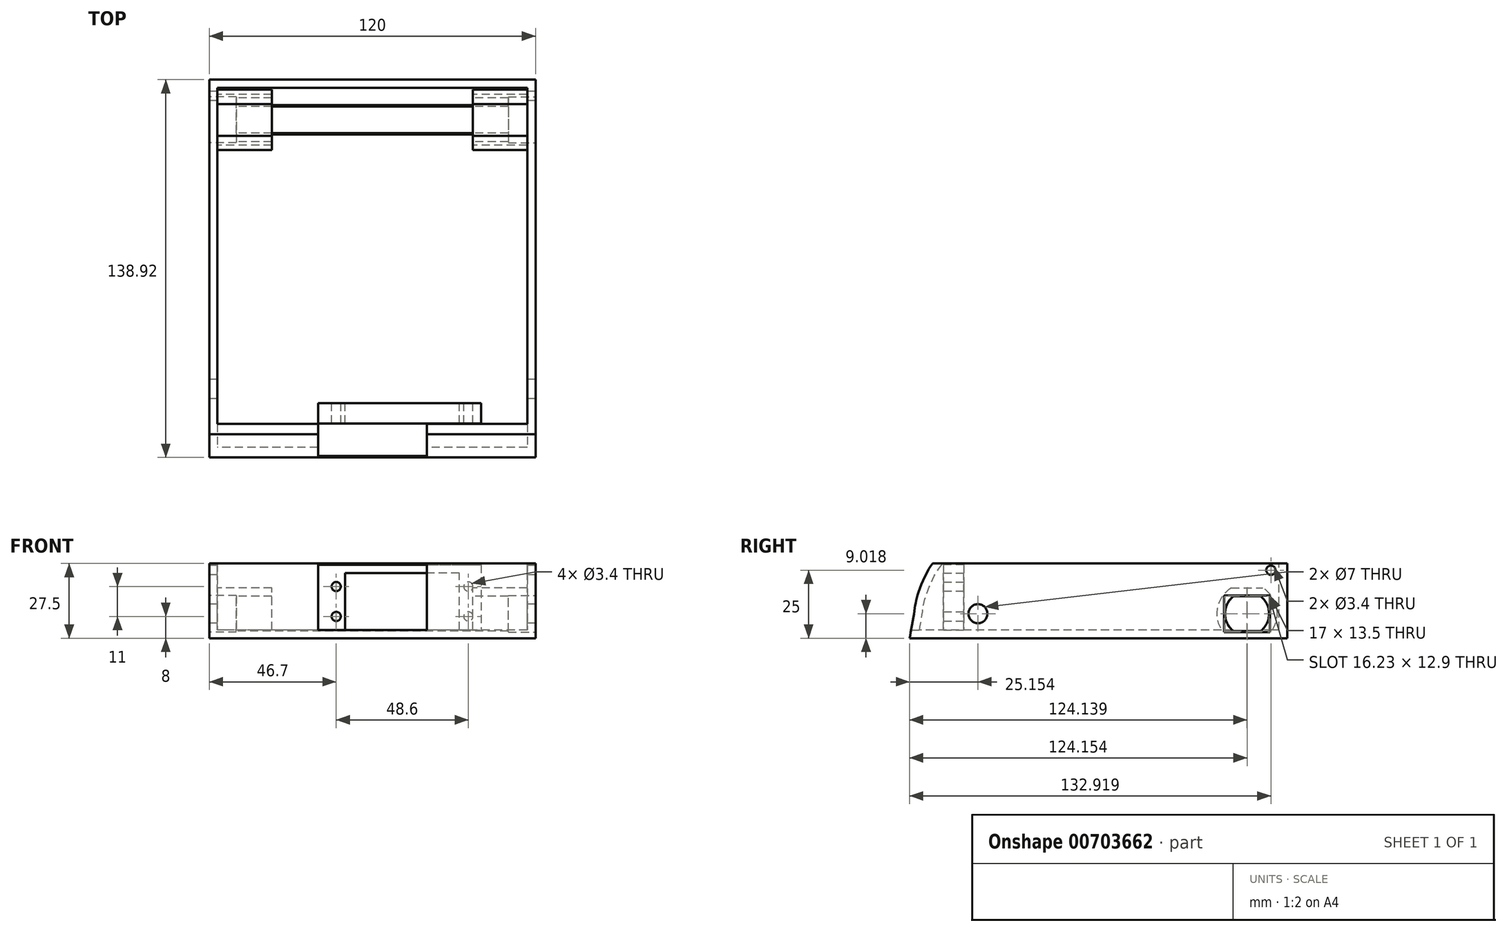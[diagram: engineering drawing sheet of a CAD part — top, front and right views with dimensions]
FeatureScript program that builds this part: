
annotation { "Feature Type Name" : "Feature", "Feature Type Description" : "" }
export const myFeature = defineFeature(function(context is Context, id is Id, definition is map)
    precondition{}
    {
        {
            var Q0;
            Q0=qCreatedBy(makeId("Right.planeOp"),FACE);
            var sketch = newSketch(context, id + "F0", { "sketchPlane" : qUnion([Q0])});
            skLineSegment(sketch, "E0", {"start": v(-41, 0) * mm, "end": v(-40.96, 0) * mm});
            skLineSegment(sketch, "E1", {"start": v(97.96, 0) * mm, "end": v(97.96, 27.5) * mm});
            skLineSegment(sketch, "E2", {"start": v(83.2, 9.02) * mm, "end": v(-15.8, 9.02) * mm, "construction": true});
            skPoint(sketch, "E3", {"position": v(-15.8, 9.02) * mm});
            skLineSegment(sketch, "E4", {"start": v(78.27, 15.47) * mm, "end": v(88.1, 15.47) * mm});
            skLineSegment(sketch, "E5", {"start": v(88.1, 15.47) * mm, "end": v(88.1, 2.57) * mm, "construction": true});
            skLineSegment(sketch, "E6", {"start": v(88.1, 2.57) * mm, "end": v(78.27, 2.57) * mm});
            skArc(sketch, "E7", {"start": v(88.1, 2.57) * mm, "mid": v(91.3, 9.02) * mm, "end": v(88.1, 15.47) * mm});
            skArc(sketch, "E8", {"start": v(78.27, 15.47) * mm, "mid": v(75.07, 9.02) * mm, "end": v(78.27, 2.57) * mm});
            skPoint(sketch, "E9", {"position": v(91.96, 25) * mm});
            skLineSegment(sketch, "E10.bottom", {"start": v(97.96, 27.5) * mm, "end": v(-28.02, 27.5) * mm});
            skLineSegment(sketch, "E10.top", {"start": v(97.96, 0) * mm, "end": v(-32.25, 0) * mm});
            skLineSegment(sketch, "E10.left", {"start": v(97.96, 27.5) * mm, "end": v(97.96, 0) * mm});
            skLineSegment(sketch, "E11.bottom", {"start": v(97.96, 27.5) * mm, "end": v(91.96, 27.5) * mm, "construction": true});
            skLineSegment(sketch, "E11.top", {"start": v(97.96, 25) * mm, "end": v(91.96, 25) * mm, "construction": true});
            skLineSegment(sketch, "E11.left", {"start": v(97.96, 27.5) * mm, "end": v(97.96, 25) * mm, "construction": true});
            skLineSegment(sketch, "E11.right", {"start": v(91.96, 27.5) * mm, "end": v(91.96, 25) * mm, "construction": true});
            skLineSegment(sketch, "E12.trimOffspring", {"start": v(-32.25, 0) * mm, "end": v(97.96, 0) * mm});
            skLineSegment(sketch, "E13", {"start": v(-28.02, 27.5) * mm, "end": v(-32.48, 27.5) * mm});
            skFitSpline(sketch, "E14.trimOffspring", {"points": [v(-39.2, 9.98) * mm, v(-16.17, 42.26) * mm, v(13.43, 34.63) * mm, v(52.81, 46.98) * mm, v(101.54, 39.4) * mm], "startDerivative": vector(14.6, 154.8) * mm, "endDerivative": vector(82.89, -42.84) * mm, "construction": true});
            skFitSpline(sketch, "E15", {"points": [v(-32.48, 27.5) * mm, v(-37.99, 15.88) * mm, v(-39.2, 9.98) * mm, v(-40.96, 0) * mm], "startDerivative": vector(-16.4, -20.95) * mm, "endDerivative": vector(-4.3, -20.78) * mm});
            skLineSegment(sketch, "E16", {"start": v(-40.96, 0) * mm, "end": v(-32.25, 0) * mm});
            skLineSegment(sketch, "E17.bottom", {"start": v(-40.96, 0) * mm, "end": v(-35.91, 0) * mm});
            skSolve(sketch);
        }
        {
            var Q0;
            Q0=makeQuery(id+"F0.imprint","IMPRINT",FACE,{"disambiguationData":[TD([[makeQuery(id+"F0.imprint","IMPRINT",EDGE,{"derivedFrom":sQuery(id+"F0.wireOp",EDGE,"E4")}),1.0]])]});
            var Q1;
            {var subQ0=sQuery(id+"F0.wireOp",EDGE,"E17.bottom");Q1=makeQuery(id+"F0.imprint","IMPRINT",FACE,{"disambiguationData":[TD([[makeQuery(id+"F0.imprint","IMPRINT",EDGE,{"derivedFrom":subQ0}),1.0]])]});}
            extrude(context, id + "F1", {"entities" : qUnion([Q0, Q1]), "depth" : 120 * mm, "offsetDistance" : 25.4 * mm});
        }
        {
            var Q0;
            Q0=makeQuery(id+"F1.opExtrude","SWEPT_FACE",FACE,{"disambiguationData":[OSD([sQuery(id+"F0.wireOp",EDGE,"E10.bottom")])]});
            shell(context, id + "F2", {"entities" : qUnion([Q0]), "thickness" : 3 * mm});
        }
        {
            var Q0;
            Q0=sQuery(id+"F0.wireOp",VERTEX,"E3");
            var Q1;
            Q1=makeQuery(id+"F1.opExtrude","SWEPT_BODY",BODY,{"disambiguationData":[OSD([sQuery(id+"F0.wireOp",EDGE,"E4"),sQuery(id+"F0.wireOp",EDGE,"E6"),sQuery(id+"F0.wireOp",EDGE,"E7"),sQuery(id+"F0.wireOp",EDGE,"E8"),sQuery(id+"F0.wireOp",EDGE,"E10.bottom"),sQuery(id+"F0.wireOp",EDGE,"E10.top"),sQuery(id+"F0.wireOp",EDGE,"E10.left"),sQuery(id+"F0.wireOp",EDGE,"E10.right")])]});
            hole(context, id + "F3", {"style" : HoleStyle.SIMPLE, "endStyle" : HoleEndStyle.BLIND, "oppositeDirection" : true, "holeDiameter" : 7 * mm, "majorDiameter" : 5 * mm, "holeDepth" : 200 * mm, "isTappedThrough" : true, "tappedDepth" : 12 * mm, "tapClearance" : 3, "locations" : qUnion([Q0]), "scope" : qUnion([Q1])});
        }
        {
            var Q0;
            Q0=sQuery(id+"F0.wireOp",VERTEX,"E9");
            var Q1;
            Q1=makeQuery(id+"F1.opExtrude","SWEPT_BODY",BODY,{"disambiguationData":[OSD([sQuery(id+"F0.wireOp",EDGE,"E0"),sQuery(id+"F0.wireOp",EDGE,"E1"),sQuery(id+"F0.wireOp",EDGE,"acc88329-f66e-44b0-b4c6-be808748104b"),sQuery(id+"F0.wireOp",EDGE,"9b4011fb-e8ac-4986-8edf-912ef74731e7.bottom"),sQuery(id+"F0.wireOp",EDGE,"E4"),sQuery(id+"F0.wireOp",EDGE,"E6"),sQuery(id+"F0.wireOp",EDGE,"E7"),sQuery(id+"F0.wireOp",EDGE,"E8")])]});
            hole(context, id + "F4", {"style" : HoleStyle.SIMPLE, "endStyle" : HoleEndStyle.BLIND, "oppositeDirection" : true, "holeDiameter" : 3.4 * mm, "majorDiameter" : 5 * mm, "holeDepth" : 200 * mm, "isTappedThrough" : true, "tappedDepth" : 12 * mm, "tapClearance" : 3, "locations" : qUnion([Q0]), "scope" : qUnion([Q1])});
        }
        {
            var Q0;
            Q0=makeQuery(id+"F1.opExtrude","CAP_FACE",FACE,{"disambiguationData":[OSD([sQuery(id+"F0.wireOp",EDGE,"E0"),sQuery(id+"F0.wireOp",EDGE,"E1"),sQuery(id+"F0.wireOp",EDGE,"acc88329-f66e-44b0-b4c6-be808748104b"),sQuery(id+"F0.wireOp",EDGE,"9b4011fb-e8ac-4986-8edf-912ef74731e7.bottom"),sQuery(id+"F0.wireOp",EDGE,"E4"),sQuery(id+"F0.wireOp",EDGE,"E6"),sQuery(id+"F0.wireOp",EDGE,"E7"),sQuery(id+"F0.wireOp",EDGE,"E8")])],"isStart":false});
            var sketch = newSketch(context, id + "F5", { "sketchPlane" : qUnion([Q0])});
            skLineSegment(sketch, "E18.bottom", {"start": v(91.7, 2.27) * mm, "end": v(74.7, 2.27) * mm});
            skLineSegment(sketch, "E18.top", {"start": v(91.7, 15.77) * mm, "end": v(74.7, 15.77) * mm});
            skLineSegment(sketch, "E18.left", {"start": v(91.7, 2.27) * mm, "end": v(91.7, 15.77) * mm});
            skLineSegment(sketch, "E18.right", {"start": v(74.7, 2.27) * mm, "end": v(74.7, 15.77) * mm});
            skPoint(sketch, "E18.middle", {"position": v(83.2, 9.02) * mm});
            skSolve(sketch);
        }
        {
            var Q0;
            Q0=qSketchRegion(id+"F5",true);
            extrude(context, id + "F6", {"entities" : qUnion([Q0]), "operationType" : NewBodyOperationType.REMOVE, "oppositeDirection" : true, "depth" : 10 * mm, "offsetDistance" : 25 * mm});
        }
        {
            var Q0;
            Q0=makeQuery(id+"F0.imprint","IMPRINT",FACE,{"disambiguationData":[TD([[makeQuery(id+"F0.imprint","IMPRINT",EDGE,{"derivedFrom":sQuery(id+"F0.wireOp",EDGE,"E4")}),1.0]])]});
            var sketch = newSketch(context, id + "F7", { "sketchPlane" : qUnion([Q0])});
            skLineSegment(sketch, "E19.bottom", {"start": v(91.7, 15.77) * mm, "end": v(74.7, 15.77) * mm});
            skLineSegment(sketch, "E19.top", {"start": v(91.7, 2.27) * mm, "end": v(74.7, 2.27) * mm});
            skLineSegment(sketch, "E19.left", {"start": v(91.7, 15.77) * mm, "end": v(91.7, 2.27) * mm});
            skLineSegment(sketch, "E19.right", {"start": v(74.7, 15.77) * mm, "end": v(74.7, 2.27) * mm});
            skPoint(sketch, "E19.middle", {"position": v(83.2, 9.02) * mm});
            skSolve(sketch);
        }
        {
            var Q0;
            Q0=qSketchRegion(id+"F7",true);
            extrude(context, id + "F8", {"entities" : qUnion([Q0]), "operationType" : NewBodyOperationType.REMOVE, "depth" : 10 * mm, "offsetDistance" : 25 * mm});
        }
        {
            var Q0;
            Q0=makeQuery(id+"F1.opExtrude","SWEPT_FACE",FACE,{"disambiguationData":[OSD([sQuery(id+"F0.wireOp",EDGE,"E12.trimOffspring"),sQuery(id+"F0.wireOp",EDGE,"E16"),sQuery(id+"F0.wireOp",EDGE,"E17.bottom")])]});
            var sketch = newSketch(context, id + "F9", { "sketchPlane" : qUnion([Q0])});
            skLineSegment(sketch, "E20.bottom", {"start": v(0, 0) * mm, "end": v(120, 0) * mm, "construction": true});
            skLineSegment(sketch, "E20.top", {"start": v(0, -97.96) * mm, "end": v(120, -97.96) * mm, "construction": true});
            skLineSegment(sketch, "E20.left", {"start": v(0, 0) * mm, "end": v(0, -97.96) * mm, "construction": true});
            skLineSegment(sketch, "E20.right", {"start": v(120, 0) * mm, "end": v(120, -97.96) * mm, "construction": true});
            skLineSegment(sketch, "E21.bottom", {"start": v(120, -97.96) * mm, "end": v(97, -97.96) * mm, "construction": true});
            skLineSegment(sketch, "E21.top", {"start": v(120, -94.96) * mm, "end": v(97, -94.96) * mm, "construction": true});
            skLineSegment(sketch, "E21.left", {"start": v(120, -97.96) * mm, "end": v(120, -94.96) * mm, "construction": true});
            skLineSegment(sketch, "E21.right", {"start": v(97, -97.96) * mm, "end": v(97, -94.96) * mm, "construction": true});
            skLineSegment(sketch, "E22.bottom", {"start": v(0, 0) * mm, "end": v(60, 0) * mm, "construction": true});
            skLineSegment(sketch, "E22.top", {"start": v(0, 35) * mm, "end": v(60, 35) * mm, "construction": true});
            skLineSegment(sketch, "E22.left", {"start": v(0, 0) * mm, "end": v(0, 35) * mm, "construction": true});
            skLineSegment(sketch, "E22.right", {"start": v(60, 0) * mm, "end": v(60, 35) * mm, "construction": true});
            skLineSegment(sketch, "E23.bottom", {"start": v(40, 52.5) * mm, "end": v(80, 52.5) * mm});
            skLineSegment(sketch, "E23.top", {"start": v(40, 17.5) * mm, "end": v(80, 17.5) * mm});
            skLineSegment(sketch, "E23.left", {"start": v(40, 52.5) * mm, "end": v(40, 17.5) * mm});
            skLineSegment(sketch, "E23.right", {"start": v(80, 52.5) * mm, "end": v(80, 17.5) * mm});
            skPoint(sketch, "E23.middle", {"position": v(60, 35) * mm});
            skLineSegment(sketch, "E24.bottom", {"start": v(97, -94.96) * mm, "end": v(23, -94.96) * mm});
            skLineSegment(sketch, "E24.top", {"start": v(97, -69.96) * mm, "end": v(23, -69.96) * mm});
            skLineSegment(sketch, "E24.left", {"start": v(97, -94.96) * mm, "end": v(97, -69.96) * mm});
            skLineSegment(sketch, "E24.right", {"start": v(23, -94.96) * mm, "end": v(23, -69.96) * mm});
            skSolve(sketch);
        }
        {
            var Q0;
            Q0 = qSketchRegion(id + "F9", true);
            extrude(context, id + "F10", {"entities" : qUnion([Q0]), "operationType" : NewBodyOperationType.REMOVE, "oppositeDirection" : true, "depth" : 30 * mm, "offsetDistance" : 25 * mm, "hasSecondDirection" : true, "secondDirectionOppositeDirection" : true, "secondDirectionDepth" : 3 * mm});
        }
        {
            var Q0;
            Q0=makeQuery(id+"F10.boolean.opBoolean","MERGE",FACE,{"derivedFrom":[makeQuery(id+"F2.opShell","OFFSET_FACE",FACE,{"disambiguationData":[OSD([sQuery(id+"F0.wireOp",EDGE,"E12.trimOffspring"),sQuery(id+"F0.wireOp",EDGE,"E16"),sQuery(id+"F0.wireOp",EDGE,"E17.bottom")]),OD(0.0)]}),makeQuery(id+"F10.opExtrude","CAP_FACE",FACE,{"disambiguationData":[OSD([sQuery(id+"F9.wireOp",EDGE,"E23.bottom"),sQuery(id+"F9.wireOp",EDGE,"E23.top"),sQuery(id+"F9.wireOp",EDGE,"E23.left"),sQuery(id+"F9.wireOp",EDGE,"E23.right")])],"isStart":true}),makeQuery(id+"F10.opExtrude","CAP_FACE",FACE,{"disambiguationData":[OSD([sQuery(id+"F9.wireOp",EDGE,"E24.bottom"),sQuery(id+"F9.wireOp",EDGE,"E24.top"),sQuery(id+"F9.wireOp",EDGE,"E24.left"),sQuery(id+"F9.wireOp",EDGE,"E24.right")])],"isStart":true})]});
            var sketch = newSketch(context, id + "F11", { "sketchPlane" : qUnion([Q0])});
            skLineSegment(sketch, "E25.bottom", {"start": v(0, 0) * mm, "end": v(40, 0) * mm, "construction": true});
            skLineSegment(sketch, "E25.top", {"start": v(0, -21) * mm, "end": v(40, -21) * mm, "construction": true});
            skLineSegment(sketch, "E25.left", {"start": v(0, 0) * mm, "end": v(0, -21) * mm, "construction": true});
            skLineSegment(sketch, "E25.right", {"start": v(40, 0) * mm, "end": v(40, -21) * mm, "construction": true});
            skLineSegment(sketch, "E26.bottom", {"start": v(40, -21) * mm, "end": v(100, -21) * mm});
            skLineSegment(sketch, "E26.top", {"start": v(40, -28.5) * mm, "end": v(100, -28.5) * mm});
            skLineSegment(sketch, "E26.left", {"start": v(40, -21) * mm, "end": v(40, -28.5) * mm});
            skLineSegment(sketch, "E26.right", {"start": v(100, -21) * mm, "end": v(100, -28.5) * mm});
            skSolve(sketch);
        }
        {
            var Q0;
            Q0 = qSketchRegion(id + "F11", true);
            extrude(context, id + "F12", {"entities" : qUnion([Q0]), "operationType" : NewBodyOperationType.ADD, "depth" : 24 * mm, "offsetDistance" : 25 * mm});
        }
        {
            var Q0;
            Q0=makeQuery(id+"F12.opExtrude","SWEPT_FACE",FACE,{"disambiguationData":[OSD([sQuery(id+"F11.wireOp",EDGE,"E26.bottom")])]});
            var sketch = newSketch(context, id + "F13", { "sketchPlane" : qUnion([Q0])});
            skLineSegment(sketch, "E27.top", {"start": v(-71, 13.5) * mm, "end": v(-60, 13.5) * mm});
            skLineSegment(sketch, "E28", {"start": v(-100, 3) * mm, "end": v(-92, 3) * mm, "construction": true});
            skLineSegment(sketch, "E29.bottom", {"start": v(-92, 3) * mm, "end": v(-50, 3) * mm});
            skLineSegment(sketch, "E29.top", {"start": v(-92, 24) * mm, "end": v(-50, 24) * mm});
            skLineSegment(sketch, "E29.left", {"start": v(-92, 3) * mm, "end": v(-92, 24) * mm});
            skLineSegment(sketch, "E30.bottom", {"start": v(-92, 3) * mm, "end": v(-77.5, 3) * mm, "construction": true});
            skLineSegment(sketch, "E30.top", {"start": v(-92, 13.5) * mm, "end": v(-71, 13.5) * mm});
            skLineSegment(sketch, "E30.left", {"start": v(-92, 3) * mm, "end": v(-92, 13.5) * mm, "construction": true});
            skLineSegment(sketch, "E31.bottom", {"start": v(-67.67, 13.5) * mm, "end": v(-60, 13.5) * mm, "construction": true});
            skPoint(sketch, "E32.orphan", {"position": v(-82, 13.5) * mm});
            skLineSegment(sketch, "E33", {"start": v(-50, 24) * mm, "end": v(-50, 3) * mm});
            skPoint(sketch, "E34.middle", {"position": v(-71, 13.5) * mm});
            skLineSegment(sketch, "E35.bottom", {"start": v(-46.7, 8) * mm, "end": v(-95.3, 8) * mm, "construction": true});
            skLineSegment(sketch, "E35.top", {"start": v(-46.7, 19) * mm, "end": v(-95.3, 19) * mm, "construction": true});
            skLineSegment(sketch, "E35.left", {"start": v(-46.7, 8) * mm, "end": v(-46.7, 19) * mm, "construction": true});
            skLineSegment(sketch, "E35.right", {"start": v(-95.3, 8) * mm, "end": v(-95.3, 19) * mm, "construction": true});
            skPoint(sketch, "E36", {"position": v(-95.3, 19) * mm});
            skPoint(sketch, "E37", {"position": v(-95.3, 8) * mm});
            skPoint(sketch, "E38", {"position": v(-46.7, 19) * mm});
            skPoint(sketch, "E39", {"position": v(-46.7, 8) * mm});
            skCircle(sketch, "E40", {"center": v(-95.3, 19) * mm, "radius": 1.7 * mm});
            skCircle(sketch, "E41", {"center": v(-95.3, 8) * mm, "radius": 1.7 * mm});
            skCircle(sketch, "E42", {"center": v(-46.7, 19) * mm, "radius": 1.7 * mm});
            skCircle(sketch, "E43", {"center": v(-46.7, 8) * mm, "radius": 1.7 * mm});
            skSolve(sketch);
        }
        {
            var Q0;
            Q0 = qSketchRegion(id + "F13", true);
            extrude(context, id + "F14", {"entities" : qUnion([Q0]), "operationType" : NewBodyOperationType.REMOVE, "oppositeDirection" : true, "depth" : 9 * mm, "offsetDistance" : 25 * mm});
        }
    });
